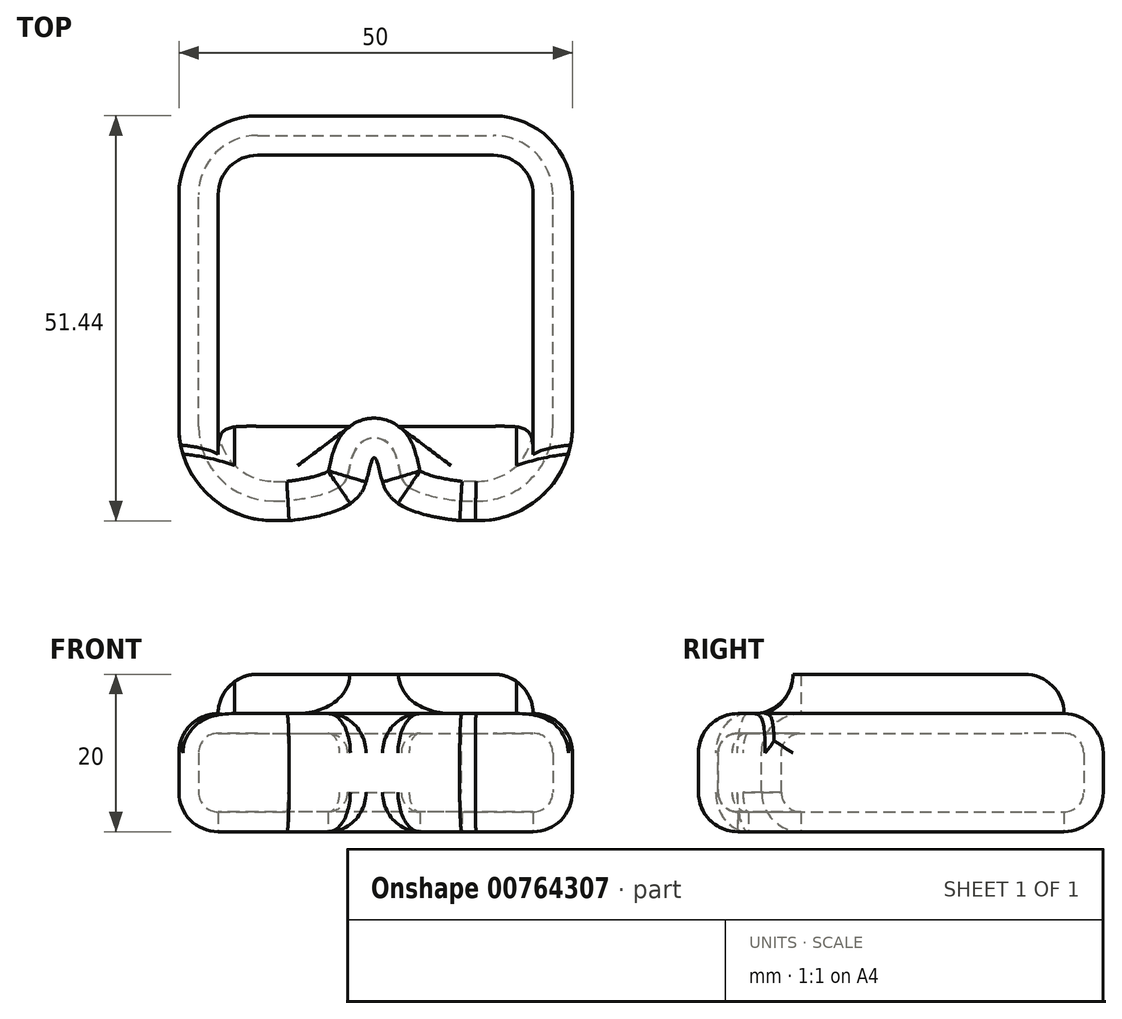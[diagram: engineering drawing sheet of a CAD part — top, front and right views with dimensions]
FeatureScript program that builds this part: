
annotation { "Feature Type Name" : "Feature", "Feature Type Description" : "" }
export const myFeature = defineFeature(function(context is Context, id is Id, definition is map)
    precondition{}
    {
        {
            var Q0;
            Q0=qCreatedBy(makeId("Top.planeOp"),FACE);
            var sketch = newSketch(context, id + "F0", { "sketchPlane" : qUnion([Q0])});
            skLineSegment(sketch, "E0.bottom", {"start": v(-15, 25.72) * mm, "end": v(15, 25.72) * mm});
            skLineSegment(sketch, "E0.top", {"start": v(-13, -25.72) * mm, "end": v(-11, -25.72) * mm});
            skLineSegment(sketch, "E0.left", {"start": v(-25, 15.72) * mm, "end": v(-25, -13.72) * mm});
            skLineSegment(sketch, "E0.right", {"start": v(25, 15.72) * mm, "end": v(25, -13.72) * mm});
            skPoint(sketch, "E0.middle", {"position": v(0, 0) * mm});
            skPoint(sketch, "E1.visualSharp", {"position": v(-25, 25.72) * mm});
            skArc(sketch, "E1.filletArc", {"start": v(-15, 25.72) * mm, "mid": v(-22.07, 22.79) * mm, "end": v(-25, 15.72) * mm});
            skPoint(sketch, "E2.visualSharp", {"position": v(25, 25.72) * mm});
            skArc(sketch, "E2.filletArc", {"start": v(25, 15.72) * mm, "mid": v(22.07, 22.79) * mm, "end": v(15, 25.72) * mm});
            skPoint(sketch, "E3.visualSharp", {"position": v(-25, -25.72) * mm});
            skArc(sketch, "E3.filletArc", {"start": v(-25, -13.72) * mm, "mid": v(-21.49, -22.2) * mm, "end": v(-13, -25.72) * mm});
            skPoint(sketch, "E4.visualSharp", {"position": v(25, -25.72) * mm});
            skArc(sketch, "E4.filletArc", {"start": v(12.68, -25.71) * mm, "mid": v(21.37, -22.31) * mm, "end": v(25, -13.72) * mm});
            skPoint(sketch, "E5.newPointB", {"position": v(12.9, -25.72) * mm});
            skPoint(sketch, "E6", {"position": v(-0.93, -19.68) * mm});
            skPoint(sketch, "E7", {"position": v(0.58, -19.68) * mm});
            skLineSegment(sketch, "E8", {"start": v(12.68, -25.71) * mm, "end": v(10.68, -25.71) * mm});
            skFitSpline(sketch, "E9", {"points": [v(-11, -25.72) * mm, v(-0.93, -19.68) * mm, v(-0.18, -17.68) * mm, v(0.58, -19.68) * mm, v(10.68, -25.71) * mm], "startDerivative": vector(77.07, 8.58) * mm, "endDerivative": vector(77, -8.54) * mm});
            skSolve(sketch);
        }
        {
            var Q0;
            Q0=makeQuery(id+"F0.imprint","IMPRINT",FACE,{"disambiguationData":[TD([[makeQuery(id+"F0.imprint","IMPRINT",EDGE,{"derivedFrom":sQuery(id+"F0.wireOp",EDGE,"E0.bottom")}),-1.0]])]});
            extrude(context, id + "F1", {"entities" : qUnion([Q0]), "depth" : 10 * mm, "offsetDistance" : 25 * mm});
        }
        {
            var Q0;
            Q0=makeQuery(id+"F1.opExtrude","CAP_FACE",FACE,{"disambiguationData":[OSD([sQuery(id+"F0.wireOp",EDGE,"E0.bottom"),sQuery(id+"F0.wireOp",EDGE,"E0.top"),sQuery(id+"F0.wireOp",EDGE,"E0.left"),sQuery(id+"F0.wireOp",EDGE,"E0.right"),sQuery(id+"F0.wireOp",EDGE,"E1.filletArc"),sQuery(id+"F0.wireOp",EDGE,"E2.filletArc"),sQuery(id+"F0.wireOp",EDGE,"E3.filletArc"),sQuery(id+"F0.wireOp",EDGE,"E4.filletArc"),sQuery(id+"F0.wireOp",EDGE,"E8"),sQuery(id+"F0.wireOp",EDGE,"E9")])],"isStart":true});
            fillet(context, id + "F2", {"entities" : qUnion([Q0]), "radius" : 5 * mm, "tangentPropagation" : true, "allowEdgeOverflow" : false});
        }
        {
            var Q0;
            Q0=makeQuery(id+"F1.opExtrude","CAP_FACE",FACE,{"disambiguationData":[OSD([sQuery(id+"F0.wireOp",EDGE,"E0.bottom"),sQuery(id+"F0.wireOp",EDGE,"E0.top"),sQuery(id+"F0.wireOp",EDGE,"E0.left"),sQuery(id+"F0.wireOp",EDGE,"E0.right"),sQuery(id+"F0.wireOp",EDGE,"E1.filletArc"),sQuery(id+"F0.wireOp",EDGE,"E2.filletArc"),sQuery(id+"F0.wireOp",EDGE,"E3.filletArc"),sQuery(id+"F0.wireOp",EDGE,"E4.filletArc"),sQuery(id+"F0.wireOp",EDGE,"E8"),sQuery(id+"F0.wireOp",EDGE,"E9")])],"isStart":false});
            extrude(context, id + "F3", {"entities" : qUnion([Q0]), "operationType" : NewBodyOperationType.ADD, "depth" : 5 * mm, "offsetDistance" : 25 * mm});
        }
        {
            var Q0;
            Q0=makeQuery(id+"F3.opExtrude","CAP_FACE",FACE,{"disambiguationData":[OSD([sQuery(id+"F0.wireOp",EDGE,"E0.bottom"),sQuery(id+"F0.wireOp",EDGE,"E0.top"),sQuery(id+"F0.wireOp",EDGE,"E0.left"),sQuery(id+"F0.wireOp",EDGE,"E0.right"),sQuery(id+"F0.wireOp",EDGE,"E1.filletArc"),sQuery(id+"F0.wireOp",EDGE,"E2.filletArc"),sQuery(id+"F0.wireOp",EDGE,"E3.filletArc"),sQuery(id+"F0.wireOp",EDGE,"E4.filletArc"),sQuery(id+"F0.wireOp",EDGE,"E8"),sQuery(id+"F0.wireOp",EDGE,"E9")])],"isStart":false});
            fillet(context, id + "F4", {"entities" : qUnion([Q0]), "radius" : 5 * mm, "tangentPropagation" : true, "allowEdgeOverflow" : false});
        }
        {
            var Q0;
            Q0=makeQuery(id+"F1.opExtrude","CAP_FACE",FACE,{"disambiguationData":[OSD([sQuery(id+"F0.wireOp",EDGE,"E0.bottom"),sQuery(id+"F0.wireOp",EDGE,"E0.top"),sQuery(id+"F0.wireOp",EDGE,"E0.left"),sQuery(id+"F0.wireOp",EDGE,"E0.right"),sQuery(id+"F0.wireOp",EDGE,"E1.filletArc"),sQuery(id+"F0.wireOp",EDGE,"E2.filletArc"),sQuery(id+"F0.wireOp",EDGE,"E3.filletArc"),sQuery(id+"F0.wireOp",EDGE,"E4.filletArc"),sQuery(id+"F0.wireOp",EDGE,"E8"),sQuery(id+"F0.wireOp",EDGE,"E9")])],"isStart":true});
            shell(context, id + "F5", {"entities" : qUnion([Q0]), "thickness" : 2.5 * mm});
        }
        {
            var Q0;
            Q0=makeQuery(id+"F3.opExtrude","CAP_FACE",FACE,{"disambiguationData":[OSD([sQuery(id+"F0.wireOp",EDGE,"E0.bottom"),sQuery(id+"F0.wireOp",EDGE,"E0.top"),sQuery(id+"F0.wireOp",EDGE,"E0.left"),sQuery(id+"F0.wireOp",EDGE,"E0.right"),sQuery(id+"F0.wireOp",EDGE,"E1.filletArc"),sQuery(id+"F0.wireOp",EDGE,"E2.filletArc"),sQuery(id+"F0.wireOp",EDGE,"E3.filletArc"),sQuery(id+"F0.wireOp",EDGE,"E4.filletArc"),sQuery(id+"F0.wireOp",EDGE,"E8"),sQuery(id+"F0.wireOp",EDGE,"E9")])],"isStart":false});
            var sketch = newSketch(context, id + "F6", { "sketchPlane" : qUnion([Q0])});
            skLineSegment(sketch, "E10", {"start": v(-20, 15.72) * mm, "end": v(-20, -13.72) * mm});
            skLineSegment(sketch, "E11", {"start": v(-20, -13.72) * mm, "end": v(20, -13.72) * mm});
            skLineSegment(sketch, "E12", {"start": v(20, -13.72) * mm, "end": v(20, 15.72) * mm});
            skPoint(sketch, "E13.endSnap0", {"position": v(-18.54, 19.25) * mm});
            skPoint(sketch, "E13.end.orphan", {"position": v(-20, 19.25) * mm});
            skLineSegment(sketch, "E14", {"start": v(15, 20.72) * mm, "end": v(-15, 20.72) * mm});
            skLineSegment(sketch, "E15", {"start": v(-20, 15.72) * mm, "end": v(-20, 15.72) * mm});
            skPoint(sketch, "E16.visualSharp", {"position": v(-20, 20.72) * mm});
            skArc(sketch, "E16.filletArc", {"start": v(-15, 20.72) * mm, "mid": v(-18.54, 19.25) * mm, "end": v(-20, 15.72) * mm});
            skPoint(sketch, "E17.visualSharp", {"position": v(20, 20.72) * mm});
            skArc(sketch, "E17.filletArc", {"start": v(20, 15.72) * mm, "mid": v(18.54, 19.25) * mm, "end": v(15, 20.72) * mm});
            skPoint(sketch, "E18", {"position": v(-3.26, -13.72) * mm});
            skPoint(sketch, "E19", {"position": v(2.9, -13.72) * mm});
            skSolve(sketch);
        }
        {
            var Q0;
            {var subQ8=sQuery(id+"F6.wireOp",EDGE,"E10");Q0=makeQuery(id+"F6.imprint","IMPRINT",FACE,{"disambiguationData":[TD([[makeQuery(id+"F6.imprint","IMPRINT",EDGE,{"derivedFrom":subQ8}),1.0]])]});}
            extrude(context, id + "F7", {"entities" : qUnion([Q0]), "operationType" : NewBodyOperationType.ADD, "depth" : 5 * mm, "offsetDistance" : 25 * mm});
        }
        {
            var Q0;
            {var subQ0=sQuery(id+"F0.wireOp",EDGE,"E9");var subQ1=sQuery(id+"F0.wireOp",EDGE,"E0.left");var subQ2=sQuery(id+"F0.wireOp",EDGE,"E3.filletArc");var subQ3=sQuery(id+"F0.wireOp",EDGE,"E0.top");var subQ6=sQuery(id+"F0.wireOp",EDGE,"E8");var subQ7=sQuery(id+"F0.wireOp",EDGE,"E4.filletArc");var subQ8=sQuery(id+"F0.wireOp",EDGE,"E2.filletArc");var subQ9=sQuery(id+"F0.wireOp",EDGE,"E1.filletArc");var subQ10=sQuery(id+"F0.wireOp",EDGE,"E0.right");var subQ11=sQuery(id+"F0.wireOp",EDGE,"E0.bottom");var subQ12=makeQuery(id+"F3.opExtrude","CAP_FACE",FACE,{"disambiguationData":[OSD([subQ11,subQ3,subQ1,subQ10,subQ9,subQ8,subQ2,subQ7,subQ6,subQ0])],"isStart":false});Q0=makeQuery(id+"F7.boolean.opBoolean","SPLIT",FACE,{"disambiguationData":[TD([makeQuery(id+"F4.opFillet","BLEND_FACE",FACE,{"disambiguationData":[OSD([subQ3])]})])],"derivedFrom":subQ12});}
            fillet(context, id + "F8", {"entities" : qUnion([Q0]), "radius" : 5 * mm, "tangentPropagation" : true, "allowEdgeOverflow" : false});
        }
        {
            var Q0;
            {var subQ0=sQuery(id+"F0.wireOp",EDGE,"E9");var subQ2=sQuery(id+"F0.wireOp",EDGE,"E4.filletArc");var subQ3=sQuery(id+"F0.wireOp",EDGE,"E8");var subQ4=sQuery(id+"F0.wireOp",EDGE,"E0.right");var subQ5=sQuery(id+"F0.wireOp",EDGE,"E3.filletArc");var subQ6=sQuery(id+"F0.wireOp",EDGE,"E2.filletArc");var subQ7=sQuery(id+"F0.wireOp",EDGE,"E1.filletArc");var subQ8=sQuery(id+"F0.wireOp",EDGE,"E0.left");var subQ9=sQuery(id+"F0.wireOp",EDGE,"E0.top");var subQ10=sQuery(id+"F0.wireOp",EDGE,"E0.bottom");var subQ12=makeQuery(id+"F3.opExtrude","CAP_FACE",FACE,{"disambiguationData":[OSD([subQ10,subQ9,subQ8,subQ4,subQ7,subQ6,subQ5,subQ2,subQ3,subQ0])],"isStart":false});Q0=makeQuery(id+"F7.boolean.opBoolean","SPLIT",FACE,{"disambiguationData":[TD([makeQuery(id+"F4.opFillet","BLEND_FACE",FACE,{"disambiguationData":[OSD([subQ4])]})])],"derivedFrom":subQ12});}
            fillet(context, id + "F9", {"entities" : qUnion([Q0]), "radius" : 5 * mm, "tangentPropagation" : true, "allowEdgeOverflow" : false});
        }
        {
            var Q0;
            Q0=makeQuery(id+"F7.opExtrude","CAP_EDGE",EDGE,{"disambiguationData":[OSD([sQuery(id+"F6.wireOp",EDGE,"E14")])],"isStart":false});
            fillet(context, id + "F10", {"entities" : qUnion([Q0]), "radius" : 5 * mm, "tangentPropagation" : true, "allowEdgeOverflow" : false});
        }
    });
